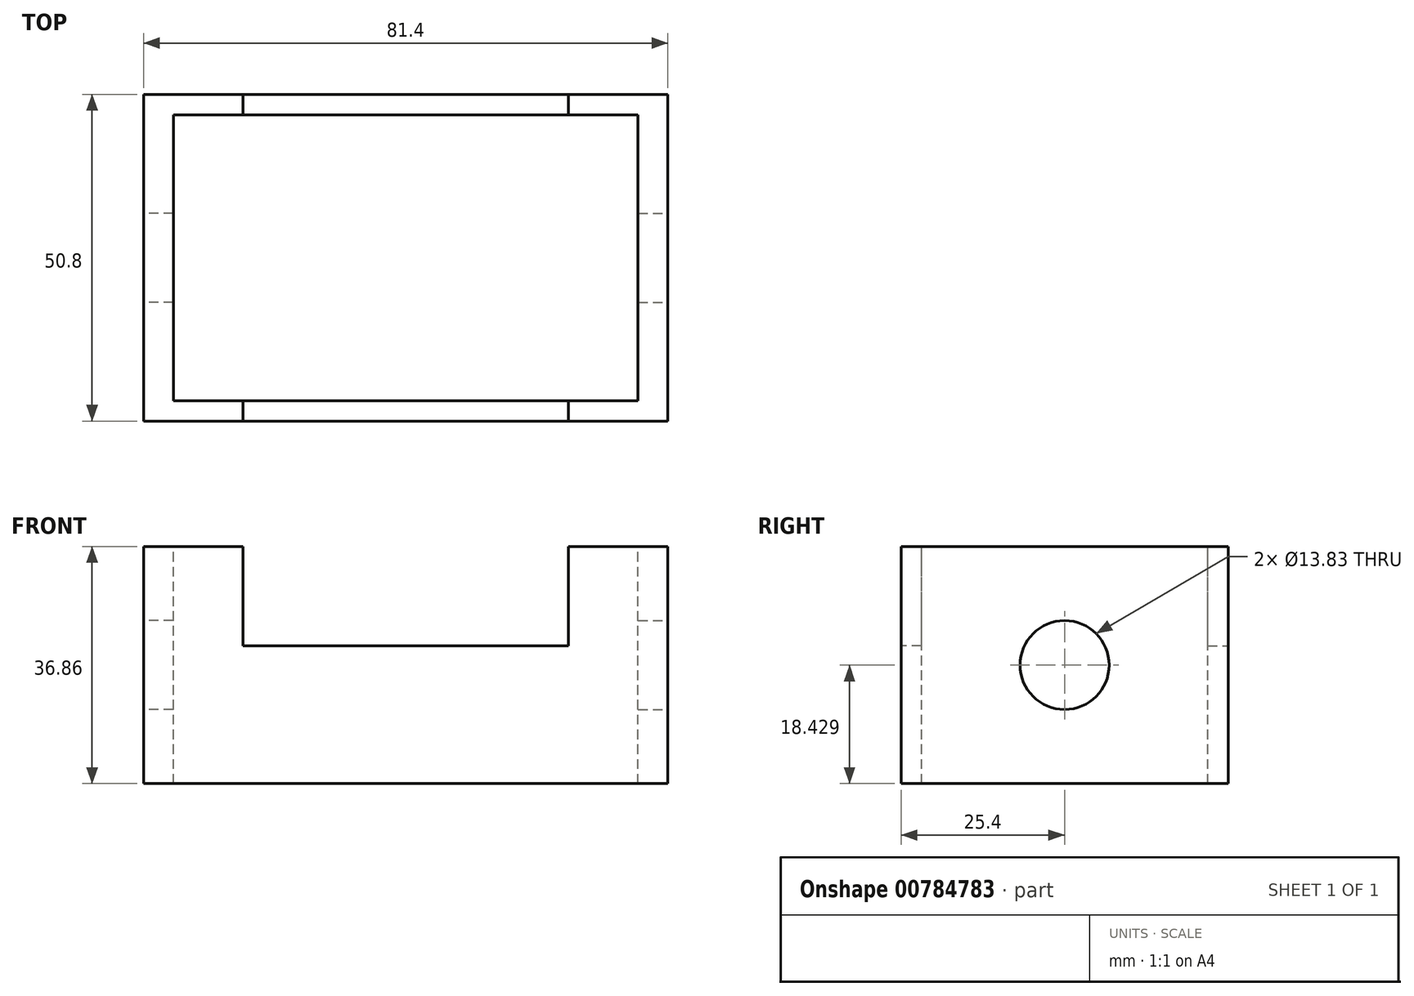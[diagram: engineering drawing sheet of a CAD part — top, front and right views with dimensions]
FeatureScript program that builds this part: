
annotation { "Feature Type Name" : "Feature", "Feature Type Description" : "" }
export const myFeature = defineFeature(function(context is Context, id is Id, definition is map)
    precondition{}
    {
        {
            var Q0;
            Q0=qCreatedBy(makeId("Front.planeOp"),FACE);
            var sketch = newSketch(context, id + "F0", { "sketchPlane" : qUnion([Q0])});
            skLineSegment(sketch, "E0", {"start": v(0, 0) * mm, "end": v(0, 21.42) * mm});
            skLineSegment(sketch, "E1.MirrorCS", {"start": v(25.26, 21.42) * mm, "end": v(25.26, 36.86) * mm});
            skLineSegment(sketch, "E2.MirrorCS", {"start": v(0, 21.42) * mm, "end": v(25.26, 21.42) * mm});
            skLineSegment(sketch, "E3.MirrorCS", {"start": v(40.7, 0) * mm, "end": v(0, 0) * mm});
            skLineSegment(sketch, "E4.MirrorCS", {"start": v(40.7, 36.86) * mm, "end": v(40.7, 0) * mm});
            skLineSegment(sketch, "E5.MirrorCS", {"start": v(25.26, 36.86) * mm, "end": v(40.7, 36.86) * mm});
            skLineSegment(sketch, "E6.MirrorCS", {"start": v(36.1, 36.86) * mm, "end": v(36.1, 0) * mm});
            skSolve(sketch);
        }
        {
            var Q0;
            {var subQ0=sQuery(id+"F0.wireOp",EDGE,"vR8pUBbG-NIrN-BiX1-eZbs-J3fbIdUpVyGV");Q0=makeQuery(id+"F0.imprint","IMPRINT",FACE,{"disambiguationData":[TD([[makeQuery(id+"F0.imprint","IMPRINT",EDGE,{"derivedFrom":subQ0}),1.0]])]});}
            var Q1;
            {var subQ0=sQuery(id+"F0.wireOp",EDGE,"E4.MirrorCS");Q1=makeQuery(id+"F0.imprint","IMPRINT",FACE,{"disambiguationData":[TD([[makeQuery(id+"F0.imprint","IMPRINT",EDGE,{"derivedFrom":subQ0}),-1.0]])]});}
            var Q2;
            {var subQ2=sQuery(id+"F0.wireOp",EDGE,"E0");Q2=makeQuery(id+"F0.imprint","IMPRINT",FACE,{"disambiguationData":[TD([[makeQuery(id+"F0.imprint","IMPRINT",EDGE,{"derivedFrom":subQ2}),1.0]])]});}
            var Q3;
            {var subQ1=sQuery(id+"F0.wireOp",EDGE,"E0");Q3=makeQuery(id+"F0.imprint","IMPRINT",FACE,{"disambiguationData":[TD([[makeQuery(id+"F0.imprint","IMPRINT",EDGE,{"derivedFrom":subQ1}),-1.0]])]});}
            extrude(context, id + "F1", {"entities" : qUnion([Q0, Q1, Q2, Q3]), "depth" : 3.17 * mm, "offsetDistance" : 25.4 * mm});
        }
        {
            var Q0;
            {var subQ0=sQuery(id+"F0.wireOp",EDGE,"E4.MirrorCS");Q0=makeQuery(id+"F0.imprint","IMPRINT",FACE,{"disambiguationData":[TD([[makeQuery(id+"F0.imprint","IMPRINT",EDGE,{"derivedFrom":subQ0}),-1.0]])]});}
            extrude(context, id + "F2", {"entities" : qUnion([Q0]), "operationType" : NewBodyOperationType.ADD, "depth" : 25.4 * mm, "offsetDistance" : 25.4 * mm});
        }
        {
            var Q0;
            {var subQ0=sQuery(id+"F0.wireOp",EDGE,"E4.MirrorCS");Q0=makeQuery(id+"F2.boolean.opBoolean","MERGE",FACE,{"derivedFrom":[makeQuery(id+"F1.opExtrude","SWEPT_FACE",FACE,{"disambiguationData":[OSD([subQ0])]}),makeQuery(id+"F2.opExtrude","SWEPT_FACE",FACE,{"disambiguationData":[OSD([subQ0])]})]});}
            var sketch = newSketch(context, id + "F3", { "sketchPlane" : qUnion([Q0])});
            skArc(sketch, "E7", {"start": v(-25.4, 11.51) * mm, "mid": v(-18.48, 18.43) * mm, "end": v(-25.4, 25.34) * mm});
            skSolve(sketch);
        }
        {
            var Q0;
            {var subQ0=sQuery(id+"F3.wireOp",EDGE,"E7");Q0=makeQuery(id+"F3.imprint","IMPRINT",FACE,{"disambiguationData":[TD([[makeQuery(id+"F3.imprint","IMPRINT",EDGE,{"derivedFrom":subQ0}),1.0]])]});}
            extrude(context, id + "F4", {"entities" : qUnion([Q0]), "operationType" : NewBodyOperationType.REMOVE, "oppositeDirection" : true, "depth" : 6.35 * mm, "offsetDistance" : 25.4 * mm});
        }
        {
            var Q0;
            Q0=makeQuery(id+"F1.opExtrude","SWEPT_BODY",BODY,{"disambiguationData":[OSD([sQuery(id+"F0.wireOp",EDGE,"E0"),sQuery(id+"F0.wireOp",EDGE,"E1.MirrorCS"),sQuery(id+"F0.wireOp",EDGE,"E2.MirrorCS"),sQuery(id+"F0.wireOp",EDGE,"E3.MirrorCS"),sQuery(id+"F0.wireOp",EDGE,"E4.MirrorCS"),sQuery(id+"F0.wireOp",EDGE,"E5.MirrorCS")])]});
            var Q1;
            Q1=qCreatedBy(makeId("Right.planeOp"),FACE);
            mirror(context, id + "F5", {"operationType" : NewBodyOperationType.ADD, "entities" : qUnion([Q0]), "mirrorPlane" : qUnion([Q1])});
        }
        {
            var Q0;
            Q0=makeQuery(id+"F1.opExtrude","SWEPT_BODY",BODY,{"disambiguationData":[OSD([sQuery(id+"F0.wireOp",EDGE,"E0"),sQuery(id+"F0.wireOp",EDGE,"E1.MirrorCS"),sQuery(id+"F0.wireOp",EDGE,"E2.MirrorCS"),sQuery(id+"F0.wireOp",EDGE,"E3.MirrorCS"),sQuery(id+"F0.wireOp",EDGE,"E4.MirrorCS"),sQuery(id+"F0.wireOp",EDGE,"E5.MirrorCS")])]});
            var Q1;
            {var subQ0=sQuery(id+"F0.wireOp",EDGE,"E4.MirrorCS");var subQ1=sQuery(id+"F0.wireOp",EDGE,"E3.MirrorCS");var subQ2=sQuery(id+"F0.wireOp",EDGE,"E6.MirrorCS");Q1=makeQuery(id+"F4.boolean.opBoolean","SPLIT",FACE,{"disambiguationData":[TD([makeQuery(id+"F1.opExtrude","SWEPT_FACE",FACE,{"disambiguationData":[OSD([subQ1])]})])],"derivedFrom":makeQuery(id+"F2.opExtrude","CAP_FACE",FACE,{"disambiguationData":[OSD([subQ1,subQ0,sQuery(id+"F0.wireOp",EDGE,"E5.MirrorCS"),subQ2])],"isStart":false})});}
            mirror(context, id + "F6", {"operationType" : NewBodyOperationType.ADD, "entities" : qUnion([Q0]), "mirrorPlane" : qUnion([Q1])});
        }
    });
